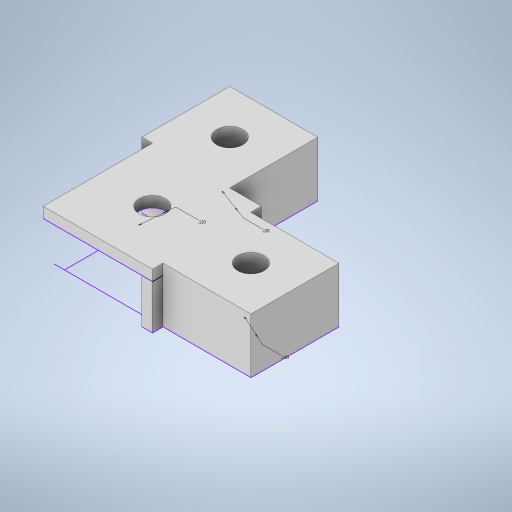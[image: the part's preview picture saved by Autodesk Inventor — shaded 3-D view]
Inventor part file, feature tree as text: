
AUTODESK INVENTOR PART (.ipt)
format: ipt  version: 2024 (Build 280153000, 153)  size: 267,776 bytes
history: native  units: in
note: dims shown in document units (in); Inventor stores cm internally (conversion verified against a paired STEP export)
features: extrude x4, hole x3, sketch x2
ambient origin geometry x8: Origin, YZ Plane, XZ Plane, XY Plane, X Axis, Y Axis, Z Axis, Center Point
bodies: Solid1 (feature_tree)
feature tree (9):
  sketch  "Sketch1"  dims[d0=0.202in d1=0.0in d2=0.048in d3=0.0in]
  extrude  "Extrusion1"  Depth=0.048in TaperAngle=0.0deg
  sketch  "Sketch2"  dims[d4=0.12in d5=0.12in d6=0.75in d7=0.375in d8=0.25in d9=0.5635in d10=1.0in d11=0.8108in d12=0.25in d13=0.0in d14=0.25in d15=0.0in d16=0.12in d17=0.12in d18=0.12in d19=0.75in d20=0.375in d21=0.25in d22=0.5635in d23=1.0in d24=0.8108in d25=0.12in d26=0.75in d27=0.375in d28=0.25in d29=0.5635in d30=1.0in d31=0.8108in]
  extrude  "Extrusion2"  Depth=0.25in TaperAngle=0.0deg
  hole  "Hole1"  [1 undecoded]
  extrude  "Extrusion3"  Depth=0.25in
  extrude  "Extrusion4"  Depth=0.25in
  hole  "Hole2"  [1 undecoded]
  hole  "Hole3"  [1 undecoded]
note: 3 required parameter values undecoded (feature->parameter linkage not recoverable at this tier; creation-order binding heuristic only, values carry confidence <= 0.55)
